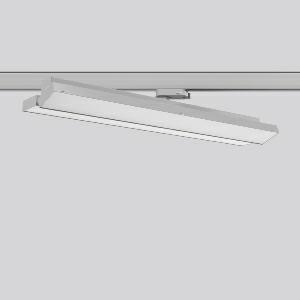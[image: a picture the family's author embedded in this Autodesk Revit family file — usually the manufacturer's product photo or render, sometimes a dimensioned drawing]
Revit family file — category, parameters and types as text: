
# Revit family: tx-move_742164_004_2_76_3731
name_source: partatom
category: Lighting Fixtures
units: mm (PartAtom-declared; Revit-internal decimal feet)

## family parameters
Cut with Voids When Loaded = No
Host = Face
Light Source = No
Part Type = Normal
Room Calculation Point = No
Round Connector Dimension = Use Diameter
Shared = No

## types (1)
- MultiLumen 1 (1 x LED Modul 927, 1775 lm, 2700)
    Apparent Load = 38 VA
    CIE Flux Codes = 47 79 96 100 100
    Color Rendering = 92
    Color Temperature = 2700
    Default Elevation = 1800 mm
    Description = Series: TX-MOVE
Multifunctional surface-mounted spotlight for area lighting. Very flat design. Housing: sheet steel, powder-coated. Rotation range: 356°. Swivel range: 90°. Consistent alignment possible with visible tilt scale. High-efficiency LED units with flush-mounted opal diffuser made of non-yellowing PMMA. Symmetrical wide beam light distribution. Best colour rendering with CRI >90 for fresh products and coloured textiles. With adapter for RZB 3-circuit DALI tracks. Suitable for Track on ceiling. MultiLumen: Luminous flux adjustable in 3 steps. Factory setting is the highest luminous flux. Environmentally friendly and resource-saving due to replaceable and recyclable components. 
Colour: silver, matt (approx. RAL 9006)
Length: 570 mm
Width: 119 mm
Height: 88 mm
Lamp: LED
Socket: without socket
Colour temperature: 2700K
Colour rendering index (CRI): 90
System power: 38 W
Rated luminous flux: 3550 lm
Luminous efficiency: 93 lm/W
System power 2: 51 W
Rated luminous flux 2: 4650 lm
Luminous efficiency 2: 91 lm/W
System power 3: 62 W
Rated luminous flux 3: 5500 lm
Luminous efficiency 3: 89 lm/W
Control gear: Dimmable EVG, DALI
Protection class: I
Type of protection: IP 20
    Height = 75 mm
    Lamp = 1 x LED Modul 927
    Lamp Light Flux = 1775 lm
    Lamp count = 1
    Length = 569 mm
    Lifetime = 50000 h
    Luminous efficacy = 93 lm/W
    Manufacturer = RZB
    ModVariant = No
    Model = 742164.004.2.76
    Mounting Place = Ceiling
    Mounting Type = Surface mounted
    Number of Poles = 1
    OnlyDefault = Yes
    Power Factor = 1
    Product Name = TX-MOVE
    Product group = Track mounted projectors
    ProductGroupID = 301
    Protection Class = Protection class I
    Protection Degree = IP 20
    RLX_Detail_Level = 1
    RLX_Emergency_Light_Flux = 0 lm
    RLX_Emergency_Type = 0
    RLX_Emergency_Type_DB = No
    RlxData = <blob elided: 32333 chars, md5=1b1a497a>
    Socket = socket
    Standby Power = 0 W
    System Light Flux = 3550 lm
    System Power = 38 W
    Type Comments = MultiLumen 1
    Type Image = 742164.004.jpg
    URL = http://relux.com
    VarID = multilumen_1
    Voltage = 0 V
    Weight = 0.00 kg
    Width = 119 mm

## geometry (parser evidence)
native form markers: Blend x4, Sweep x12
no freeform markers — native parametric forms only
